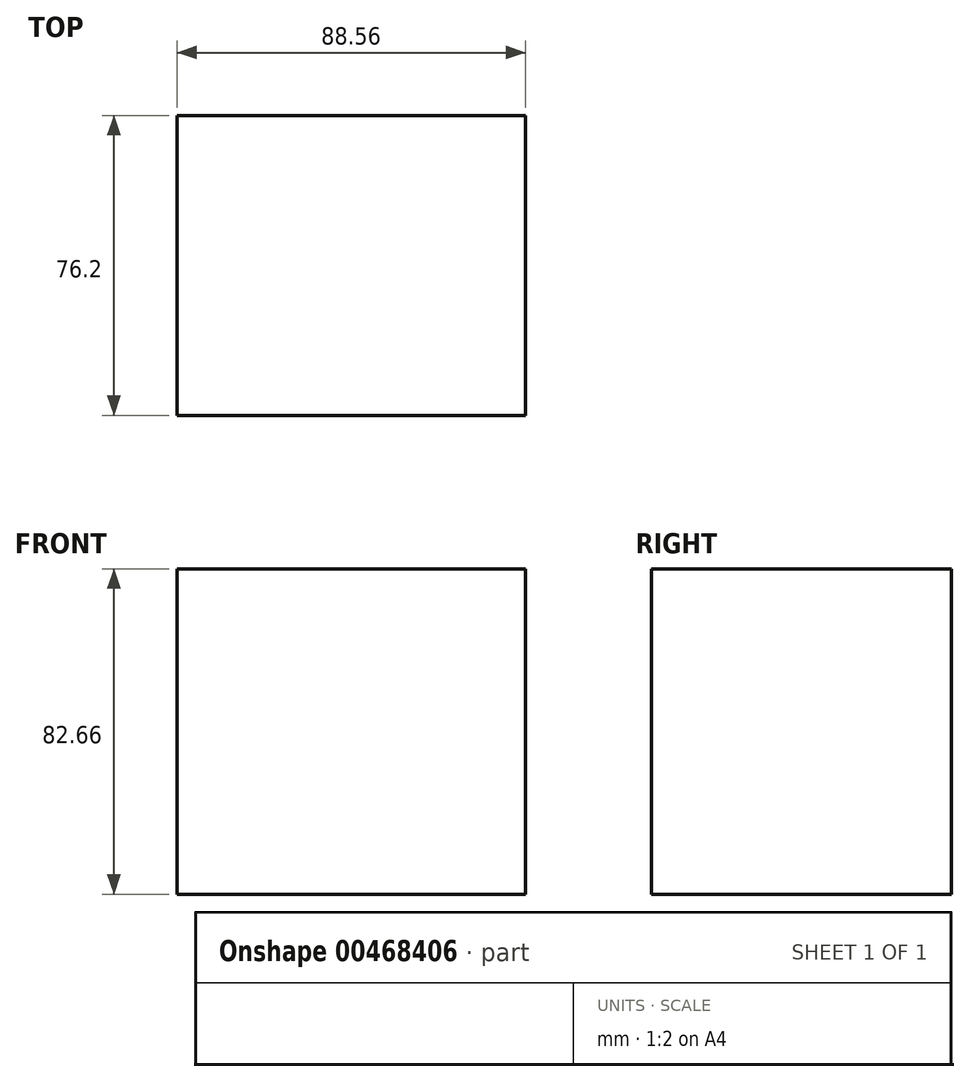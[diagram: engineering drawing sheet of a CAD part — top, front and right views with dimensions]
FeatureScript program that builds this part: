
annotation { "Feature Type Name" : "Feature", "Feature Type Description" : "" }
export const myFeature = defineFeature(function(context is Context, id is Id, definition is map)
    precondition{}
    {
        {
            var Q0;
            Q0=qCreatedBy(makeId("Front.planeOp"),FACE);
            var sketch = newSketch(context, id + "F0", { "sketchPlane" : qUnion([Q0])});
            skLineSegment(sketch, "E0.bottom", {"start": v(44.28, 41.33) * mm, "end": v(-44.28, 41.33) * mm});
            skLineSegment(sketch, "E0.top", {"start": v(44.28, -41.33) * mm, "end": v(-44.28, -41.33) * mm});
            skLineSegment(sketch, "E0.left", {"start": v(44.28, 41.33) * mm, "end": v(44.28, -41.33) * mm});
            skLineSegment(sketch, "E0.right", {"start": v(-44.28, 41.33) * mm, "end": v(-44.28, -41.33) * mm});
            skPoint(sketch, "E0.middle", {"position": v(0, 0) * mm});
            skSolve(sketch);
        }
        {
            var Q0;
            Q0=makeQuery(id+"F0.imprint","IMPRINT",FACE,{"disambiguationData":[TD([[makeQuery(id+"F0.imprint","IMPRINT",EDGE,{"derivedFrom":sQuery(id+"F0.wireOp",EDGE,"E0.bottom")}),1.0]])]});
            extrude(context, id + "F1", {"entities" : qUnion([Q0]), "depth" : 76.2 * mm});
        }
    });
